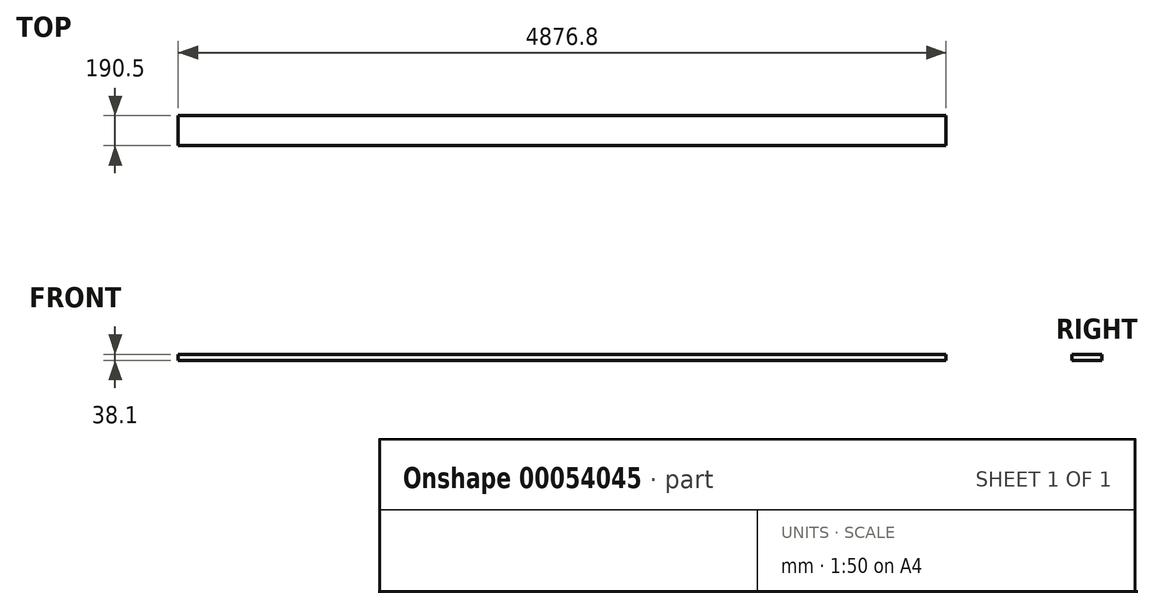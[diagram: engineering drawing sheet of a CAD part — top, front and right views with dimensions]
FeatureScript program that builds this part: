
annotation { "Feature Type Name" : "Feature", "Feature Type Description" : "" }
export const myFeature = defineFeature(function(context is Context, id is Id, definition is map)
    precondition{}
    {
        {
            var Q0;
            Q0=qCreatedBy(makeId("Right.planeOp"),FACE);
            var sketch = newSketch(context, id + "F0", { "sketchPlane" : qUnion([Q0])});
            skLineSegment(sketch, "E0.bottom", {"start": v(0, 0) * mm, "end": v(190.5, 0) * mm});
            skLineSegment(sketch, "E0.top", {"start": v(0, 38.1) * mm, "end": v(190.5, 38.1) * mm});
            skLineSegment(sketch, "E0.left", {"start": v(0, 0) * mm, "end": v(0, 38.1) * mm});
            skLineSegment(sketch, "E0.right", {"start": v(190.5, 0) * mm, "end": v(190.5, 38.1) * mm});
            skSolve(sketch);
        }
        {
            var Q0;
            Q0=makeQuery(id+"F0.imprint","IMPRINT",FACE,{"disambiguationData":[TD([[makeQuery(id+"F0.imprint","IMPRINT",EDGE,{"derivedFrom":sQuery(id+"F0.wireOp",EDGE,"E0.bottom")}),1.0]])]});
            extrude(context, id + "F1", {"entities" : qUnion([Q0]), "depth" : 4876.8 * mm});
        }
    });
